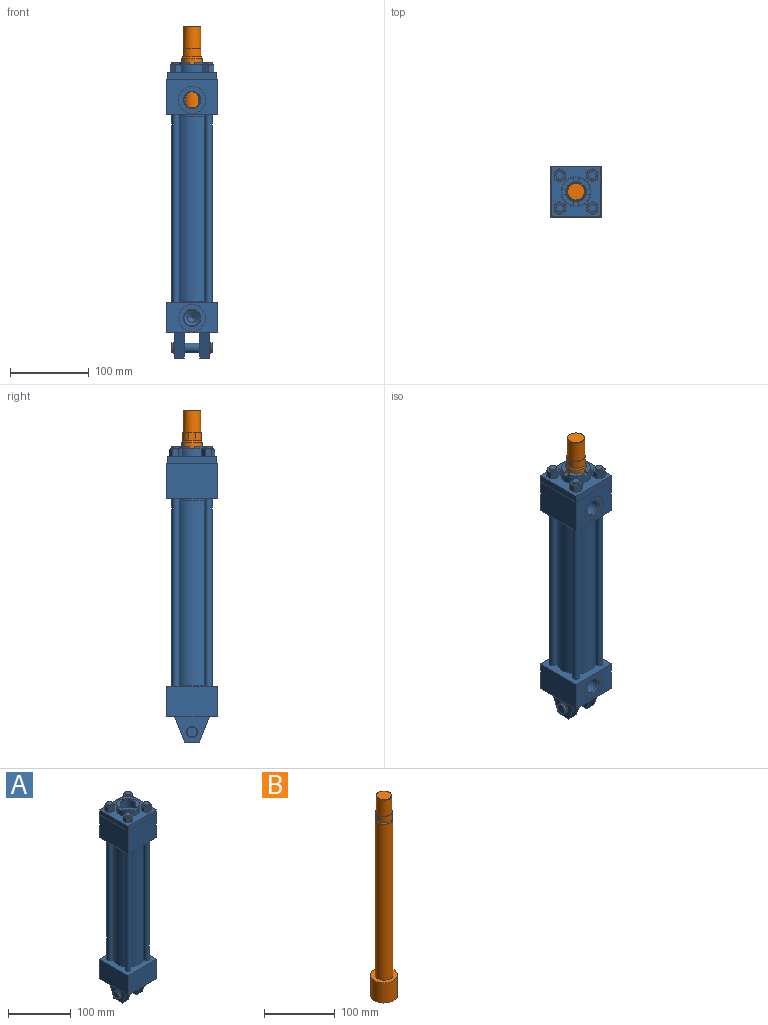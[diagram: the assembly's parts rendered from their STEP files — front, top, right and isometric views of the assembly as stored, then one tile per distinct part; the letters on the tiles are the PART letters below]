
ASSEMBLY  parts=2 mates=1
PART A: 164 faces, bbox 64.2x64.2x375.3 mm
  f0: cylinder r=24.26mm len=235.08mm, axis (0,0,-1), area 35828.4mm2, adj f29,f30
  f1: cylinder r=21.81mm len=43.62mm, axis (0,0,1), area 208.8mm2, adj f29,f31
  f2: cylinder r=21.81mm len=43.62mm, axis (0,0,1), area 208.8mm2, adj f30,f32
  f3: cylinder r=4.76mm len=238.13mm, axis (0,0,1), area 7125.6mm2, adj f31,f32
  f4: cylinder r=4.76mm len=238.13mm, axis (0,0,1), area 7125.6mm2, adj f31,f32
  f5: cylinder r=4.76mm len=238.13mm, axis (0,0,1), area 7125.6mm2, adj f31,f32
  f6: cylinder r=4.76mm len=238.13mm, axis (0,0,1), area 7125.6mm2, adj f31,f32
  f7: cylinder r=17.07mm len=34.14mm, axis (0,1,0), area 109mm2, adj f35,f51
  f8: cylinder r=17.07mm len=34.14mm, axis (0,1,0), area 109mm2, adj f38,f56
  f9: cylinder r=7.16mm len=14.33mm, axis (-1,0,0), area 46.9mm2, adj f44,f60
  f10: cylinder r=6.36mm len=19.05mm, axis (1,0,0), area 761.6mm2, adj f46,f47
  f11: cylinder r=7.16mm len=14.33mm, axis (1,0,0), area 46.9mm2, adj f49,f61
  f12: cone r=10.92mm half-angle=15deg, axis (0,1,0), area 174.7mm2, adj f14,f51
  f13: cone r=10.92mm half-angle=15deg, axis (0,1,0), area 174.7mm2, adj f16,f56
  f14: cylinder r=10.24mm len=20.47mm, axis (0,1,0), area 1112.5mm2, adj f12,f19
  f15: cylinder r=19.04mm len=38.07mm, axis (0,0,-1), area 1139.3mm2, adj f59,f86
  f16: cylinder r=10.24mm len=20.47mm, axis (0,1,0), area 1079.1mm2, adj f13,f20,f21,f111
  f17: cylinder r=6.36mm len=12.73mm, axis (1,0,0), area 133mm2, adj f60,f112
  f18: cylinder r=6.36mm len=12.73mm, axis (1,0,0), area 133mm2, adj f61,f113
  f19: cone r=10.24mm half-angle=59deg, axis (0,1,0), area 245.5mm2, adj f14,f22
  f20: cylinder r=12.7mm len=66.68mm, axis (0,0,1), area 4932.2mm2, adj f16,f21,f86,f111,f114,f115,f117,f118
  f21: cone r=10.24mm half-angle=59deg, axis (0,1,0), area 26.4mm2, adj f16,f20
  f22: cylinder r=6.15mm len=12.29mm, axis (0,1,0), area 440.7mm2, adj f19,f23
  f23: cone r=6.15mm half-angle=59deg, axis (0,1,0), area 138.5mm2, adj f22
  f24: cylinder r=19.05mm len=238.13mm, axis (0,0,1), area 28502.3mm2, adj f150,f159
  f25: cylinder r=4.76mm len=9.53mm, axis (0,0,1), area 95mm2, adj f155,f160
  f26: cylinder r=4.76mm len=9.53mm, axis (0,0,1), area 95mm2, adj f156,f161
  f27: cylinder r=4.76mm len=9.53mm, axis (0,0,1), area 95mm2, adj f157,f162
  f28: cylinder r=4.76mm len=9.53mm, axis (0,0,1), area 95mm2, adj f158,f163
  f29: plane 48.51x48.51mm, normal (0,0,-1), area 354.2mm2, adj f0,f1
  f30: plane 48.51x48.51mm, normal (0,0,1), area 354.2mm2, adj f0,f2
  f31: plane 63.5x63.5mm, normal (0,0,1), area 2252.9mm2, adj f1,f3,f4,f5,f6,f33,f34,f35
  f32: plane 63.5x63.5mm, normal (0,0,-1), area 2252.9mm2, adj f2,f3,f4,f5,f6,f37,f38,f39
  f33: plane 63.5x38.1mm, normal (0,-1,0), area 2419.3mm2, adj f31,f34,f36,f41
  f34: plane 63.5x38.1mm, normal (-1,0,0), area 2419.3mm2, adj f31,f33,f35,f41
  f35: plane 63.5x38.1mm, normal (0,1,0), area 1504.1mm2, adj f7,f31,f34,f36,f41
  f36: plane 63.5x38.1mm, normal (1,0,0), area 2419.3mm2, adj f31,f33,f35,f41
  f37: plane 63.5x44.45mm, normal (-1,0,0), area 2822.6mm2, adj f32,f38,f40,f42
  f38: plane 63.5x44.45mm, normal (0,1,0), area 1907.3mm2, adj f8,f32,f37,f39,f42
  f39: plane 63.5x44.45mm, normal (1,0,0), area 2822.6mm2, adj f32,f38,f40,f42
  f40: plane 63.5x44.45mm, normal (0,-1,0), area 2822.6mm2, adj f32,f37,f39,f42
  f41: plane 63.5x63.5mm, normal (0,0,-1), area 2904.5mm2, adj f33,f34,f35,f36,f43,f44,f45,f46
  f42: plane 63.5x63.5mm, normal (0,0,1), area 32.2mm2, adj f37,f38,f39,f40,f52,f53,f54,f55
  f43: plane 31.75x12.7mm, normal (0,-0.93,-0.37), area 434.2mm2, adj f41,f44,f46,f57
  f44: plane 44.4x31.75mm, normal (-1,0,0), area 846.1mm2, adj f9,f41,f43,f45,f57
  f45: plane 31.75x12.7mm, normal (0,0.93,-0.37), area 434.2mm2, adj f41,f44,f46,f57
  f46: plane 44.4x31.75mm, normal (1,0,0), area 880.1mm2, adj f10,f41,f43,f45,f57
  f47: plane 44.4x31.75mm, normal (-1,0,0), area 880.1mm2, adj f10,f41,f48,f50,f58
  f48: plane 31.75x12.7mm, normal (0,0.93,-0.37), area 434.2mm2, adj f41,f47,f49,f58
  f49: plane 44.4x31.75mm, normal (1,0,0), area 846.1mm2, adj f11,f41,f48,f50,f58
  f50: plane 31.75x12.7mm, normal (0,-0.93,-0.37), area 434.2mm2, adj f41,f47,f49,f58
  f51: plane 34.14x34.14mm, normal (0,1,0), area 540.9mm2, adj f7,f12
  f52: plane 63.25x9.53mm, normal (0,1,0), area 602.4mm2, adj f42,f53,f55,f59
  f53: plane 63.25x9.53mm, normal (-1,0,0), area 602.4mm2, adj f42,f52,f54,f59
  f54: plane 63.25x9.53mm, normal (0,-1,0), area 602.4mm2, adj f42,f53,f55,f59
  f55: plane 63.25x9.53mm, normal (1,0,0), area 602.4mm2, adj f42,f52,f54,f59
  f56: plane 34.14x34.14mm, normal (0,1,0), area 540.9mm2, adj f8,f13
  f57: plane 19.05x12.7mm, normal (0,0,-1), area 241.9mm2, adj f43,f44,f45,f46
  f58: plane 19.05x12.7mm, normal (0,0,-1), area 241.9mm2, adj f47,f48,f49,f50
  f59: plane 63.25x63.25mm, normal (0,0,1), area 2220.2mm2, adj f15,f52,f53,f54,f55,f62,f63,f64
  f60: plane 14.33x14.33mm, normal (-1,0,0), area 34mm2, adj f9,f17
  f61: plane 14.33x14.33mm, normal (1,0,0), area 34mm2, adj f11,f18
  f62: cone r=8.26mm half-angle=60deg, axis (0,0,1), area 5mm2, adj f59,f87,f88
  f63: cone r=8.26mm half-angle=60deg, axis (0,0,1), area 5mm2, adj f59,f87,f89
  f64: cone r=8.26mm half-angle=60deg, axis (0,0,1), area 5mm2, adj f59,f89,f90
  f65: cone r=8.26mm half-angle=60deg, axis (0,0,1), area 5mm2, adj f59,f90,f91
  f66: cone r=8.26mm half-angle=60deg, axis (0,0,1), area 5mm2, adj f59,f91,f92
  f67: cone r=8.26mm half-angle=60deg, axis (0,0,1), area 5mm2, adj f59,f88,f92
  f68: cone r=8.26mm half-angle=60deg, axis (0,0,1), area 5mm2, adj f59,f93,f94
  f69: cone r=8.26mm half-angle=60deg, axis (0,0,1), area 5mm2, adj f59,f93,f95
  f70: cone r=8.26mm half-angle=60deg, axis (0,0,1), area 5mm2, adj f59,f95,f96
  f71: cone r=8.26mm half-angle=60deg, axis (0,0,1), area 5mm2, adj f59,f96,f97
  f72: cone r=8.26mm half-angle=60deg, axis (0,0,1), area 5mm2, adj f59,f97,f98
  f73: cone r=8.26mm half-angle=60deg, axis (0,0,1), area 5mm2, adj f59,f94,f98
  f74: cone r=8.26mm half-angle=60deg, axis (0,0,1), area 5mm2, adj f59,f99,f100
  f75: cone r=8.26mm half-angle=60deg, axis (0,0,1), area 5mm2, adj f59,f99,f101
  f76: cone r=8.26mm half-angle=60deg, axis (0,0,1), area 5mm2, adj f59,f101,f102
  f77: cone r=8.26mm half-angle=60deg, axis (0,0,1), area 5mm2, adj f59,f102,f103
  f78: cone r=8.26mm half-angle=60deg, axis (0,0,1), area 5mm2, adj f59,f103,f104
  f79: cone r=8.26mm half-angle=60deg, axis (0,0,1), area 5mm2, adj f59,f100,f104
  f80: cone r=8.26mm half-angle=60deg, axis (0,0,1), area 5mm2, adj f59,f105,f106
  f81: cone r=8.26mm half-angle=60deg, axis (0,0,1), area 5mm2, adj f59,f105,f107
  f82: cone r=8.26mm half-angle=60deg, axis (0,0,1), area 5mm2, adj f59,f107,f108
  f83: cone r=8.26mm half-angle=60deg, axis (0,0,1), area 5mm2, adj f59,f108,f109
  f84: cone r=8.26mm half-angle=60deg, axis (0,0,1), area 5mm2, adj f59,f109,f110
  f85: cone r=8.26mm half-angle=60deg, axis (0,0,1), area 5mm2, adj f59,f106,f110
  f86: plane 38.07x38.07mm, normal (0,0,1), area 240.6mm2, adj f15,f20,f114,f115,f116,f117,f118,f119
  f87: plane 10.2x8.93mm, normal (-1,0,0), area 75mm2, adj f62,f63,f88,f89,f126,f127
  f88: plane 10.2x7.82mm, normal (-0.5,0.87,0), area 75mm2, adj f62,f67,f87,f92,f127,f128
  f89: plane 10.2x7.82mm, normal (-0.5,-0.87,0), area 75mm2, adj f63,f64,f87,f90,f126,f129
  f90: plane 10.2x7.82mm, normal (0.5,-0.87,0), area 75mm2, adj f64,f65,f89,f91,f129,f130
  f91: plane 10.2x8.93mm, normal (1,0,0), area 75mm2, adj f65,f66,f90,f92,f130,f131
  f92: plane 10.2x7.82mm, normal (0.5,0.87,0), area 75mm2, adj f66,f67,f88,f91,f128,f131
  f93: plane 10.2x8.93mm, normal (-1,0,0), area 75mm2, adj f68,f69,f94,f95,f132,f133
  f94: plane 10.2x7.82mm, normal (-0.5,0.87,0), area 75mm2, adj f68,f73,f93,f98,f133,f134
  f95: plane 10.2x7.82mm, normal (-0.5,-0.87,0), area 75mm2, adj f69,f70,f93,f96,f132,f135
  f96: plane 10.2x7.82mm, normal (0.5,-0.87,0), area 75mm2, adj f70,f71,f95,f97,f135,f136
  f97: plane 10.2x8.93mm, normal (1,0,0), area 75mm2, adj f71,f72,f96,f98,f136,f137
  f98: plane 10.2x7.82mm, normal (0.5,0.87,0), area 75mm2, adj f72,f73,f94,f97,f134,f137
  f99: plane 10.2x8.93mm, normal (-1,0,0), area 75mm2, adj f74,f75,f100,f101,f138,f139
  f100: plane 10.2x7.82mm, normal (-0.5,0.87,0), area 75mm2, adj f74,f79,f99,f104,f139,f140
  f101: plane 10.2x7.82mm, normal (-0.5,-0.87,0), area 75mm2, adj f75,f76,f99,f102,f138,f141
  f102: plane 10.2x7.82mm, normal (0.5,-0.87,0), area 75mm2, adj f76,f77,f101,f103,f141,f142
  f103: plane 10.2x8.93mm, normal (1,0,0), area 75mm2, adj f77,f78,f102,f104,f142,f143
  f104: plane 10.2x7.82mm, normal (0.5,0.87,0), area 75mm2, adj f78,f79,f100,f103,f140,f143
  f105: plane 10.2x8.93mm, normal (-1,0,0), area 75mm2, adj f80,f81,f106,f107,f144,f145
  f106: plane 10.2x7.82mm, normal (-0.5,0.87,0), area 75mm2, adj f80,f85,f105,f110,f145,f146
  f107: plane 10.2x7.82mm, normal (-0.5,-0.87,0), area 75mm2, adj f81,f82,f105,f108,f144,f147
  f108: plane 10.2x7.82mm, normal (0.5,-0.87,0), area 75mm2, adj f82,f83,f107,f109,f147,f148
  f109: plane 10.2x8.93mm, normal (1,0,0), area 75mm2, adj f83,f84,f108,f110,f148,f149
  f110: plane 10.2x7.82mm, normal (0.5,0.87,0), area 75mm2, adj f84,f85,f106,f109,f146,f149
  f111: cone r=10.24mm half-angle=59deg, axis (0,1,0), area 26.4mm2, adj f16,f20
  f112: plane 12.73x12.73mm, normal (-1,0,0), area 127.2mm2, adj f17
  f113: plane 12.73x12.73mm, normal (1,0,0), area 127.2mm2, adj f18
  f114: plane 5.68x3.18mm, normal (-1,0,0), area 18mm2, adj f20,f86,f125,f151
  f115: plane 5.68x3.18mm, normal (1,0,0), area 18mm2, adj f20,f86,f116,f152
  f116: cylinder r=18.24mm len=14.64mm, axis (0,0,-1), area 69.9mm2, adj f86,f115,f117,f152
  f117: plane 5.68x3.18mm, normal (0,-1,0), area 18mm2, adj f20,f86,f116,f152
  f118: plane 5.68x3.18mm, normal (0,1,0), area 18mm2, adj f20,f86,f119,f153
  f119: cylinder r=18.24mm len=14.64mm, axis (0,0,-1), area 69.9mm2, adj f86,f118,f120,f153
  f120: plane 5.68x3.18mm, normal (1,0,0), area 18mm2, adj f20,f86,f119,f153
  f121: plane 5.68x3.18mm, normal (-1,0,0), area 18mm2, adj f20,f86,f122,f154
  f122: cylinder r=18.24mm len=14.64mm, axis (0,0,-1), area 69.9mm2, adj f86,f121,f123,f154
  f123: plane 5.68x3.18mm, normal (0,1,0), area 18mm2, adj f20,f86,f122,f154
  f124: plane 5.68x3.18mm, normal (0,-1,0), area 18mm2, adj f20,f86,f125,f151
  f125: cylinder r=18.24mm len=14.64mm, axis (0,0,-1), area 69.9mm2, adj f86,f114,f124,f151
  f126: cone r=8.26mm half-angle=60deg, axis (0,0,-1), area 5mm2, adj f87,f89,f155
  f127: cone r=8.26mm half-angle=60deg, axis (0,0,-1), area 5mm2, adj f87,f88,f155
  f128: cone r=8.26mm half-angle=60deg, axis (0,0,-1), area 5mm2, adj f88,f92,f155
  f129: cone r=8.26mm half-angle=60deg, axis (0,0,-1), area 5mm2, adj f89,f90,f155
  f130: cone r=8.26mm half-angle=60deg, axis (0,0,-1), area 5mm2, adj f90,f91,f155
  f131: cone r=8.26mm half-angle=60deg, axis (0,0,-1), area 5mm2, adj f91,f92,f155
  f132: cone r=8.26mm half-angle=60deg, axis (0,0,-1), area 5mm2, adj f93,f95,f156
  f133: cone r=8.26mm half-angle=60deg, axis (0,0,-1), area 5mm2, adj f93,f94,f156
  f134: cone r=8.26mm half-angle=60deg, axis (0,0,-1), area 5mm2, adj f94,f98,f156
  f135: cone r=8.26mm half-angle=60deg, axis (0,0,-1), area 5mm2, adj f95,f96,f156
  f136: cone r=8.26mm half-angle=60deg, axis (0,0,-1), area 5mm2, adj f96,f97,f156
  f137: cone r=8.26mm half-angle=60deg, axis (0,0,-1), area 5mm2, adj f97,f98,f156
  f138: cone r=8.26mm half-angle=60deg, axis (0,0,-1), area 5mm2, adj f99,f101,f157
  f139: cone r=8.26mm half-angle=60deg, axis (0,0,-1), area 5mm2, adj f99,f100,f157
  f140: cone r=8.26mm half-angle=60deg, axis (0,0,-1), area 5mm2, adj f100,f104,f157
  f141: cone r=8.26mm half-angle=60deg, axis (0,0,-1), area 5mm2, adj f101,f102,f157
  f142: cone r=8.26mm half-angle=60deg, axis (0,0,-1), area 5mm2, adj f102,f103,f157
  f143: cone r=8.26mm half-angle=60deg, axis (0,0,-1), area 5mm2, adj f103,f104,f157
  f144: cone r=8.26mm half-angle=60deg, axis (0,0,-1), area 5mm2, adj f105,f107,f158
  f145: cone r=8.26mm half-angle=60deg, axis (0,0,-1), area 5mm2, adj f105,f106,f158
  f146: cone r=8.26mm half-angle=60deg, axis (0,0,-1), area 5mm2, adj f106,f110,f158
  f147: cone r=8.26mm half-angle=60deg, axis (0,0,-1), area 5mm2, adj f107,f108,f158
  f148: cone r=8.26mm half-angle=60deg, axis (0,0,-1), area 5mm2, adj f108,f109,f158
  f149: cone r=8.26mm half-angle=60deg, axis (0,0,-1), area 5mm2, adj f109,f110,f158
  f150: plane 38.1x38.1mm, normal (0,0,-1), area 633.4mm2, adj f20,f24
  f151: plane 14.64x14.64mm, normal (0,0,1), area 97.8mm2, adj f20,f114,f124,f125
  f152: plane 14.64x14.64mm, normal (0,0,1), area 97.8mm2, adj f20,f115,f116,f117
  f153: plane 14.64x14.64mm, normal (0,0,1), area 97.8mm2, adj f20,f118,f119,f120
  f154: plane 14.64x14.64mm, normal (0,0,1), area 97.8mm2, adj f20,f121,f122,f123
  f155: plane 14.29x14.29mm, normal (0,0,1), area 89.1mm2, adj f25,f126,f127,f128,f129,f130,f131
  f156: plane 14.29x14.29mm, normal (0,0,1), area 89.1mm2, adj f26,f132,f133,f134,f135,f136,f137
  f157: plane 14.29x14.29mm, normal (0,0,1), area 89.1mm2, adj f27,f138,f139,f140,f141,f142,f143
  f158: plane 14.29x14.29mm, normal (0,0,1), area 89.1mm2, adj f28,f144,f145,f146,f147,f148,f149
  f159: plane 38.1x38.1mm, normal (0,0,1), area 1140.1mm2, adj f24
  f160: plane 9.53x9.53mm, normal (0,0,1), area 71.3mm2, adj f25
  f161: plane 9.53x9.53mm, normal (0,0,1), area 71.3mm2, adj f26
  f162: plane 9.53x9.53mm, normal (0,0,1), area 71.3mm2, adj f27
  f163: plane 9.53x9.53mm, normal (0,0,1), area 71.3mm2, adj f28
PART B: 15 faces, bbox 38.1x38.1x346.1 mm
  f0: cylinder r=12.7mm len=269.88mm, axis (0,0,1), area 21535.1mm2, adj f1,f6
  f1: cone r=12.7mm half-angle=20deg, axis (0,0,-1), area 179.4mm2, adj f0,f2
  f2: cylinder r=11.91mm len=23.81mm, axis (0,0,-1), area 620.4mm2, adj f1,f7,f8,f9,f10,f11,f12
  f3: cylinder r=19.05mm len=38.1mm, axis (0,0,-1), area 4180.3mm2, adj f6,f13
  f4: cylinder r=11.11mm len=28.02mm, axis (0,0,-1), area 1956.4mm2, adj f5,f9,f12
  f5: cone r=11.11mm half-angle=45deg, axis (0,0,-1), area 53.5mm2, adj f4,f14
  f6: plane 38.1x38.1mm, normal (0,0,1), area 633.4mm2, adj f0,f3
  f7: plane 8.55x0.79mm, normal (0,0,1), area 4.6mm2, adj f2,f8
  f8: plane 9.53x8.55mm, normal (-1,0,0), area 81.4mm2, adj f2,f7,f9,f12
  f9: plane 22.23x11.91mm, normal (0,0,1), area 24.1mm2, adj f2,f4,f8,f10
  f10: plane 9.53x8.55mm, normal (1,0,0), area 81.4mm2, adj f2,f9,f11,f12
  f11: plane 8.55x0.79mm, normal (0,0,1), area 4.6mm2, adj f2,f10
  f12: plane 22.23x11.91mm, normal (0,0,1), area 24.1mm2, adj f2,f4,f8,f10
  f13: plane 38.1x38.1mm, normal (0,0,-1), area 1140.1mm2, adj f3
  f14: plane 21.11x21.11mm, normal (0,0,1), area 350.1mm2, adj f5
PLACE A rot(axis=(0,0,1),180deg) t=(0,0,107.95)mm
PLACE B rot(axis=(0,0,1),180deg) t=(0,0,147.64)mm
MATE slider B.f0 <-> A.f0  axis (0,0,1) through (0,0,134.94)mm
